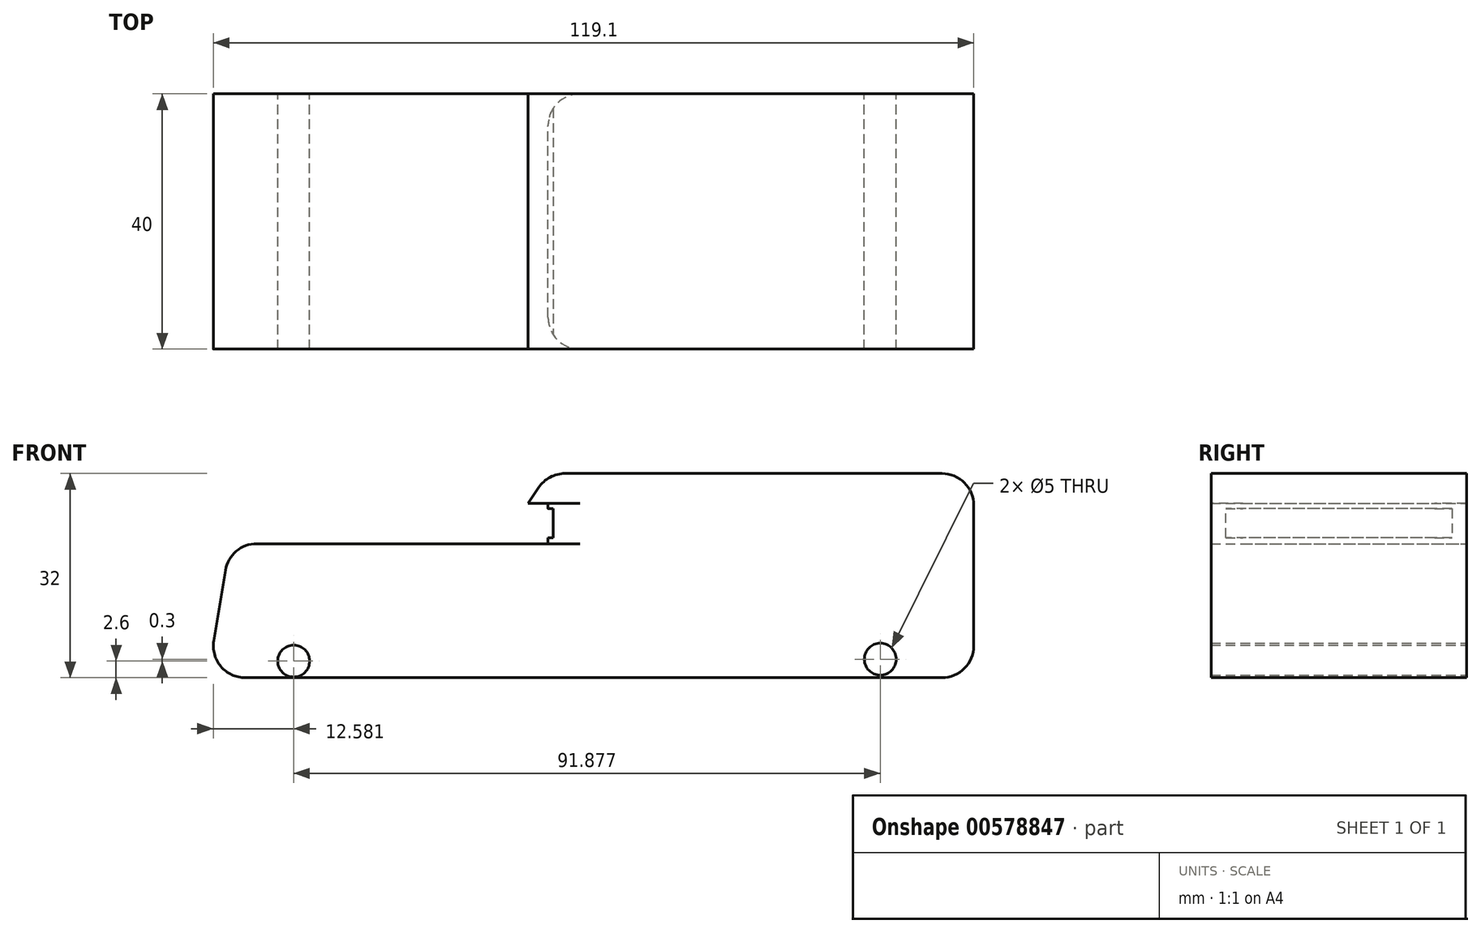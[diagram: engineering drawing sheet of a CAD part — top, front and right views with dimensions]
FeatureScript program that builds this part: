
annotation { "Feature Type Name" : "Feature", "Feature Type Description" : "" }
export const myFeature = defineFeature(function(context is Context, id is Id, definition is map)
    precondition{}
    {
        {
            var Q0;
            Q0=qCreatedBy(makeId("Front.planeOp"),FACE);
            var sketch = newSketch(context, id + "F0", { "sketchPlane" : qUnion([Q0])});
            skLineSegment(sketch, "E0", {"start": v(-53.32, 0) * mm, "end": v(66.68, 0) * mm});
            skLineSegment(sketch, "E1", {"start": v(0, 32) * mm, "end": v(0, 21) * mm});
            skLineSegment(sketch, "E2", {"start": v(0, 21) * mm, "end": v(-49.84, 21) * mm});
            skLineSegment(sketch, "E3", {"start": v(-49.84, 21) * mm, "end": v(-53.32, 0) * mm});
            skCircle(sketch, "E4", {"center": v(-39.84, 2.6) * mm, "radius": 2.5 * mm});
            skCircle(sketch, "E5", {"center": v(52.04, 2.9) * mm, "radius": 2.5 * mm});
            skLineSegment(sketch, "E6", {"start": v(0, 0) * mm, "end": v(26.6, 0) * mm});
            skLineSegment(sketch, "E7", {"start": v(66.68, 32) * mm, "end": v(0, 32) * mm});
            skLineSegment(sketch, "E8", {"start": v(0, 32) * mm, "end": v(-3.13, 27.33) * mm});
            skLineSegment(sketch, "E9", {"start": v(-3.13, 27.33) * mm, "end": v(0, 27.33) * mm});
            skLineSegment(sketch, "E10.bottom", {"start": v(0, 26.5) * mm, "end": v(4.07, 26.5) * mm});
            skLineSegment(sketch, "E10.top", {"start": v(0, 22.42) * mm, "end": v(4.07, 22.42) * mm});
            skLineSegment(sketch, "E10.left", {"start": v(0, 26.5) * mm, "end": v(0, 22.42) * mm});
            skLineSegment(sketch, "E10.right", {"start": v(4.07, 26.5) * mm, "end": v(4.07, 22.42) * mm});
            skLineSegment(sketch, "E11", {"start": v(66.68, 32) * mm, "end": v(66.68, 0) * mm});
            skSolve(sketch);
        }
        {
            var Q0;
            Q0 = qSketchRegion(id + "F0", true);
            extrude(context, id + "F1", {"entities" : qUnion([Q0]), "depth" : 40 * mm, "offsetDistance" : 25 * mm});
        }
        {
            var Q0;
            Q0=makeQuery(id+"F1.opExtrude","SWEPT_FACE",FACE,{"disambiguationData":[OSD([sQuery(id+"F0.wireOp",EDGE,"E2")])]});
            extrude(context, id + "F2", {"entities" : qUnion([Q0]), "operationType" : NewBodyOperationType.ADD, "oppositeDirection" : true, "depth" : 0.1 * mm, "offsetDistance" : 25 * mm});
        }
        {
            var Q0;
            Q0=qCreatedBy(makeId("Right.planeOp"),FACE);
            var sketch = newSketch(context, id + "F3", { "sketchPlane" : qUnion([Q0])});
            skLineSegment(sketch, "E12.bottom", {"start": v(-1.32, 26.47) * mm, "end": v(-38.7, 26.47) * mm});
            skLineSegment(sketch, "E12.top", {"start": v(-1.32, 21.95) * mm, "end": v(-38.7, 21.95) * mm});
            skLineSegment(sketch, "E12.left", {"start": v(-1.32, 26.47) * mm, "end": v(-1.32, 21.95) * mm});
            skLineSegment(sketch, "E12.right", {"start": v(-38.7, 26.47) * mm, "end": v(-38.7, 21.95) * mm});
            skSolve(sketch);
        }
        {
            var Q0;
            Q0 = qSketchRegion(id + "F3", true);
            var Q1;
            Q1=sQuery(id+"F3.wireOp",EDGE,"E12.left");
            extrude(context, id + "F4", {"entities" : qUnion([Q0]), "operationType" : NewBodyOperationType.REMOVE, "surfaceEntities" : qUnion([Q1]), "depth" : 0.8 * mm, "offsetDistance" : 25 * mm});
        }
        {
            var Q0;
            Q0=makeQuery(id+"F1.opExtrude","SWEPT_EDGE",EDGE,{"disambiguationData":[OSD([sQuery(id+"F0.wireOp",EDGE,"E2"),sQuery(id+"F0.wireOp",EDGE,"E3")])]});
            var Q1;
            Q1=makeQuery(id+"F1.opExtrude","SWEPT_EDGE",EDGE,{"disambiguationData":[OSD([sQuery(id+"F0.wireOp",EDGE,"E0"),sQuery(id+"F0.wireOp",EDGE,"E3")])]});
            var Q2;
            Q2=makeQuery(id+"F1.opExtrude","CAP_EDGE",EDGE,{"disambiguationData":[OSD([sQuery(id+"F0.wireOp",EDGE,"E1"),sQuery(id+"F0.wireOp",EDGE,"E10.left")])],"isStart":true});
            var Q3;
            Q3=makeQuery(id+"F1.opExtrude","SWEPT_EDGE",EDGE,{"disambiguationData":[OSD([sQuery(id+"F0.wireOp",EDGE,"E1"),sQuery(id+"F0.wireOp",EDGE,"E7"),sQuery(id+"F0.wireOp",EDGE,"E8")])]});
            var Q4;
            Q4=makeQuery(id+"F1.opExtrude","CAP_EDGE",EDGE,{"disambiguationData":[OSD([sQuery(id+"F0.wireOp",EDGE,"E1"),sQuery(id+"F0.wireOp",EDGE,"E10.left")])],"isStart":false});
            var Q5;
            Q5=makeQuery(id+"F1.opExtrude","SWEPT_EDGE",EDGE,{"disambiguationData":[OSD([sQuery(id+"F0.wireOp",EDGE,"E0"),sQuery(id+"F0.wireOp",EDGE,"E11")])]});
            var Q6;
            Q6=makeQuery(id+"F1.opExtrude","SWEPT_EDGE",EDGE,{"disambiguationData":[OSD([sQuery(id+"F0.wireOp",EDGE,"E7"),sQuery(id+"F0.wireOp",EDGE,"E11")])]});
            fillet(context, id + "F5", {"entities" : qUnion([Q0, Q1, Q2, Q3, Q4, Q5, Q6]), "radius" : 5 * mm, "tangentPropagation" : true, "allowEdgeOverflow" : false});
        }
    });
